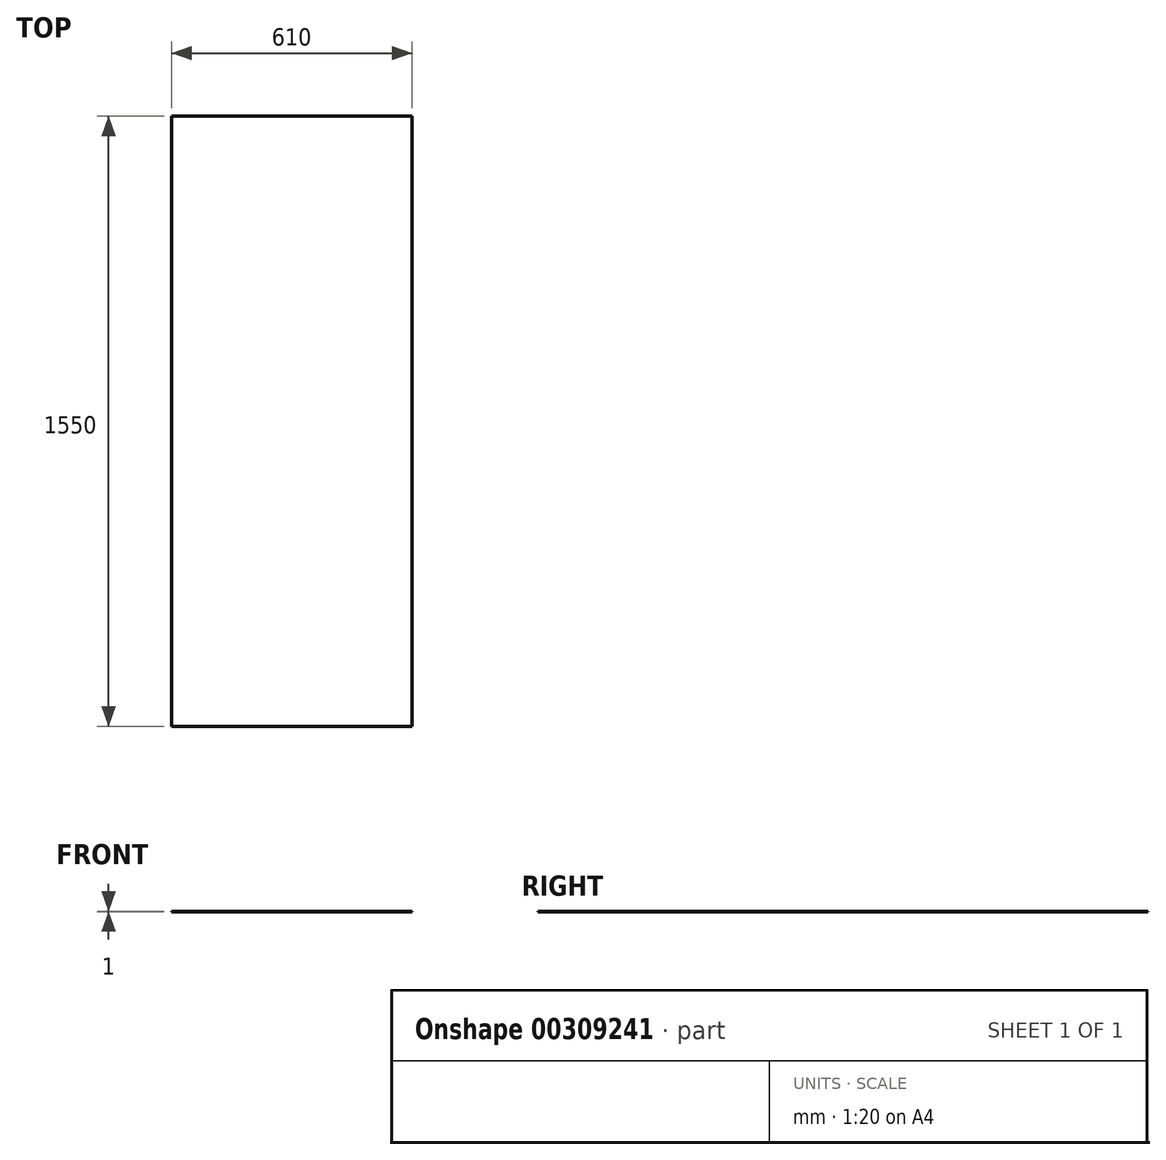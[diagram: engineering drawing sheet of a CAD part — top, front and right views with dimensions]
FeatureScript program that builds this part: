
annotation { "Feature Type Name" : "Feature", "Feature Type Description" : "" }
export const myFeature = defineFeature(function(context is Context, id is Id, definition is map)
    precondition{}
    {
        {
            var Q0;
            Q0=qCreatedBy(makeId("Right.planeOp"),FACE);
            var sketch = newSketch(context, id + "F0", { "sketchPlane" : qUnion([Q0])});
            skLineSegment(sketch, "E0.bottom", {"start": v(0, 0) * mm, "end": v(1550, 0) * mm});
            skLineSegment(sketch, "E0.top", {"start": v(0, 1) * mm, "end": v(1550, 1) * mm});
            skLineSegment(sketch, "E0.left", {"start": v(0, 0) * mm, "end": v(0, 1) * mm});
            skLineSegment(sketch, "E0.right", {"start": v(1550, 0) * mm, "end": v(1550, 1) * mm});
            skSolve(sketch);
        }
        {
            var Q0;
            Q0=makeQuery(id+"F0.imprint","IMPRINT",FACE,{"disambiguationData":[TD([[makeQuery(id+"F0.imprint","IMPRINT",EDGE,{"derivedFrom":sQuery(id+"F0.wireOp",EDGE,"E0.bottom")}),1.0]])]});
            extrude(context, id + "F1", {"entities" : qUnion([Q0]), "depth" : 610 * mm});
        }
    });
